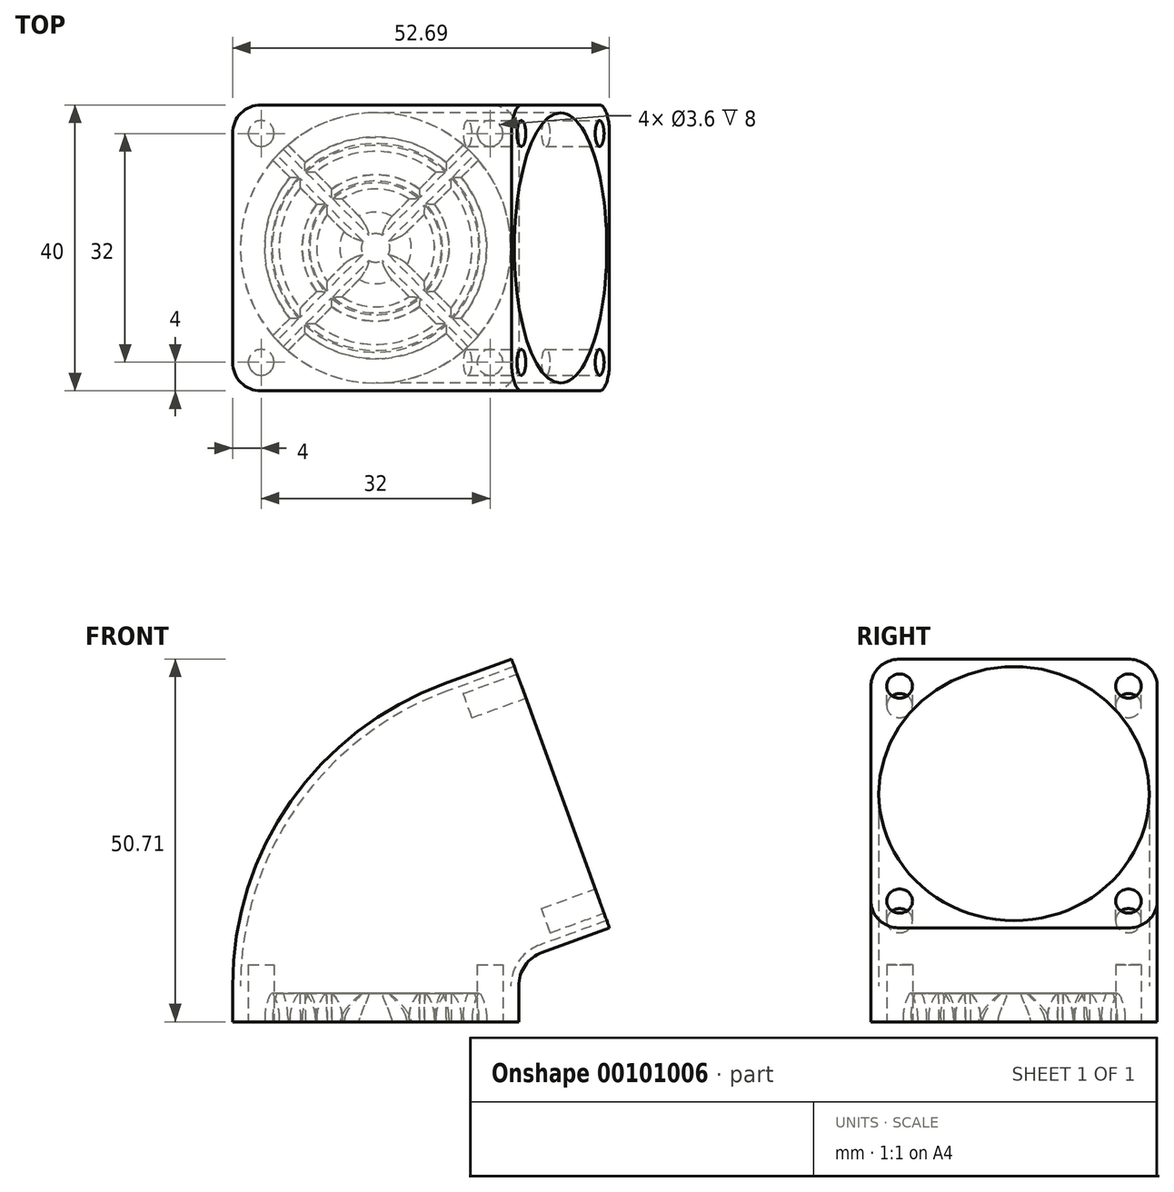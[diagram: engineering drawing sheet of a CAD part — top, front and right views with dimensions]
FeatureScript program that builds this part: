
annotation { "Feature Type Name" : "Feature", "Feature Type Description" : "" }
export const myFeature = defineFeature(function(context is Context, id is Id, definition is map)
    precondition{}
    {
        {
            var Q0;
            Q0=qCreatedBy(makeId("Top.planeOp"),FACE);
            var sketch = newSketch(context, id + "F0", { "sketchPlane" : qUnion([Q0])});
            skLineSegment(sketch, "E0.bottom", {"start": v(16, 20) * mm, "end": v(-16, 20) * mm});
            skLineSegment(sketch, "E0.top", {"start": v(16, -20) * mm, "end": v(-16, -20) * mm});
            skLineSegment(sketch, "E0.left", {"start": v(20, 16) * mm, "end": v(20, -16) * mm});
            skLineSegment(sketch, "E0.right", {"start": v(-20, 16) * mm, "end": v(-20, -16) * mm});
            skPoint(sketch, "E0.middle", {"position": v(0, 0) * mm});
            skPoint(sketch, "E1.visualSharp", {"position": v(-20, 20) * mm});
            skArc(sketch, "E1.filletArc", {"start": v(-16, 20) * mm, "mid": v(-18.83, 18.83) * mm, "end": v(-20, 16) * mm});
            skPoint(sketch, "E2.visualSharp", {"position": v(20, 20) * mm});
            skArc(sketch, "E2.filletArc", {"start": v(20, 16) * mm, "mid": v(18.83, 18.83) * mm, "end": v(16, 20) * mm});
            skPoint(sketch, "E3.visualSharp", {"position": v(20, -20) * mm});
            skArc(sketch, "E3.filletArc", {"start": v(16, -20) * mm, "mid": v(18.83, -18.83) * mm, "end": v(20, -16) * mm});
            skPoint(sketch, "E4.visualSharp", {"position": v(-20, -20) * mm});
            skArc(sketch, "E4.filletArc", {"start": v(-20, -16) * mm, "mid": v(-18.83, -18.83) * mm, "end": v(-16, -20) * mm});
            skCircle(sketch, "E5", {"center": v(16, 16) * mm, "radius": 1.8 * mm});
            skCircle(sketch, "E6", {"center": v(-16, 16) * mm, "radius": 1.8 * mm});
            skCircle(sketch, "E7", {"center": v(-16, -16) * mm, "radius": 1.8 * mm});
            skCircle(sketch, "E8", {"center": v(16, -16) * mm, "radius": 1.8 * mm});
            skCircle(sketch, "E9", {"center": v(0, 0) * mm, "radius": 18.9 * mm});
            skSolve(sketch);
        }
        {
            var Q0;
            Q0=qSketchRegion(id+"F0",true);
            extrude(context, id + "F1", {"entities" : qUnion([Q0]), "depth" : 5 * mm});
        }
        {
            var Q0;
            Q0=qCreatedBy(makeId("Top.planeOp"),FACE);
            var sketch = newSketch(context, id + "F2", { "sketchPlane" : qUnion([Q0])});
            skCircle(sketch, "E10", {"center": v(0, 0) * mm, "radius": 5 * mm});
            skCircle(sketch, "E11", {"center": v(0, 0) * mm, "radius": 8.25 * mm});
            skCircle(sketch, "E12", {"center": v(0, 0) * mm, "radius": 10.25 * mm});
            skCircle(sketch, "E13", {"center": v(0, 0) * mm, "radius": 15.5 * mm});
            skCircle(sketch, "E14", {"center": v(0, 0) * mm, "radius": 13.5 * mm});
            skLineSegment(sketch, "E15", {"start": v(-19.89, 17.77) * mm, "end": v(17.77, -19.89) * mm});
            skLineSegment(sketch, "E16", {"start": v(17.77, -19.89) * mm, "end": v(19.89, -17.77) * mm});
            skLineSegment(sketch, "E17", {"start": v(19.89, -17.77) * mm, "end": v(-17.77, 19.89) * mm});
            skLineSegment(sketch, "E18", {"start": v(-17.77, 19.89) * mm, "end": v(-19.89, 17.77) * mm});
            skLineSegment(sketch, "E19", {"start": v(17.77, 19.89) * mm, "end": v(19.89, 17.77) * mm});
            skLineSegment(sketch, "E20", {"start": v(19.89, 17.77) * mm, "end": v(-17.77, -19.89) * mm});
            skLineSegment(sketch, "E21", {"start": v(-17.77, -19.89) * mm, "end": v(-19.89, -17.77) * mm});
            skLineSegment(sketch, "E22", {"start": v(-19.89, -17.77) * mm, "end": v(17.77, 19.89) * mm});
            skLineSegment(sketch, "E23", {"start": v(0, 0) * mm, "end": v(0, 27.68) * mm, "construction": true});
            skLineSegment(sketch, "E24", {"start": v(0, 0) * mm, "end": v(18.83, 18.83) * mm, "construction": true});
            skLineSegment(sketch, "E25", {"start": v(0, 0) * mm, "end": v(-18.83, 18.83) * mm, "construction": true});
            skSolve(sketch);
        }
        {
            var Q0;
            Q0=qCreatedBy(makeId("Top.planeOp"),FACE);
            var sketch = newSketch(context, id + "F3", { "sketchPlane" : qUnion([Q0])});
            skArc(sketch, "E26.0", {"start": v(-4.43, 2.31) * mm, "mid": v(3.54, -3.54) * mm, "end": v(-2.31, 4.43) * mm});
            skArc(sketch, "E26.1", {"start": v(-6.8, 4.68) * mm, "mid": v(-8.25, 0) * mm, "end": v(-6.8, -4.68) * mm});
            skArc(sketch, "E26.2", {"start": v(-6.1, -8.23) * mm, "mid": v(0, -10.25) * mm, "end": v(6.1, -8.23) * mm});
            skArc(sketch, "E26.3", {"start": v(10.55, -8.43) * mm, "mid": v(13.5, 0) * mm, "end": v(10.55, 8.43) * mm});
            skArc(sketch, "E26.4", {"start": v(11.97, -9.85) * mm, "mid": v(15.5, 0) * mm, "end": v(11.97, 9.85) * mm});
            skLineSegment(sketch, "E26.5", {"start": v(14.38, 12.26) * mm, "end": v(11.97, 9.85) * mm});
            skLineSegment(sketch, "E26.6", {"start": v(-14.38, -12.26) * mm, "end": v(-11.97, -9.85) * mm});
            skLineSegment(sketch, "E26.7", {"start": v(14.38, -12.26) * mm, "end": v(11.97, -9.85) * mm});
            skLineSegment(sketch, "E26.8", {"start": v(-14.38, 12.26) * mm, "end": v(-11.97, 9.85) * mm});
            skLineSegment(sketch, "E27.trimOffspring", {"start": v(-2.31, -4.43) * mm, "end": v(-4.68, -6.8) * mm});
            skLineSegment(sketch, "E28.trimOffspring", {"start": v(2.31, -4.43) * mm, "end": v(4.68, -6.8) * mm});
            skLineSegment(sketch, "E29.trimOffspring", {"start": v(2.31, 4.43) * mm, "end": v(4.68, 6.8) * mm});
            skLineSegment(sketch, "E30.trimOffspring", {"start": v(-2.31, 4.43) * mm, "end": v(-4.68, 6.8) * mm});
            skArc(sketch, "E31.0", {"start": v(-14.38, -12.26) * mm, "mid": v(-13.36, -13.36) * mm, "end": v(-12.26, -14.38) * mm});
            skPoint(sketch, "E32.orphan", {"position": v(-17.77, 19.89) * mm});
            skPoint(sketch, "E33.orphan", {"position": v(-19.89, 17.77) * mm});
            skPoint(sketch, "E34.orphan", {"position": v(19.89, 17.77) * mm});
            skPoint(sketch, "E35.orphan", {"position": v(17.77, 19.89) * mm});
            skArc(sketch, "E36.trimOffspring", {"start": v(-12.26, 14.38) * mm, "mid": v(-13.36, 13.36) * mm, "end": v(-14.38, 12.26) * mm});
            skArc(sketch, "E37.trimOffspring", {"start": v(14.38, 12.26) * mm, "mid": v(13.36, 13.36) * mm, "end": v(12.26, 14.38) * mm});
            skArc(sketch, "E38.trimOffspring", {"start": v(12.26, -14.38) * mm, "mid": v(13.36, -13.36) * mm, "end": v(14.38, -12.26) * mm});
            skLineSegment(sketch, "E39.trimOffspring", {"start": v(10.55, -8.43) * mm, "end": v(8.23, -6.1) * mm});
            skLineSegment(sketch, "E40.trimOffspring", {"start": v(9.85, -11.97) * mm, "end": v(12.26, -14.38) * mm});
            skLineSegment(sketch, "E41.trimOffspring", {"start": v(-9.85, -11.97) * mm, "end": v(-12.26, -14.38) * mm});
            skArc(sketch, "E42.trimOffspring", {"start": v(-8.43, -10.55) * mm, "mid": v(0, -13.5) * mm, "end": v(8.43, -10.55) * mm});
            skLineSegment(sketch, "E43.trimOffspring", {"start": v(-10.55, -8.43) * mm, "end": v(-8.23, -6.1) * mm});
            skPoint(sketch, "E44.orphan", {"position": v(-17.77, -19.89) * mm});
            skPoint(sketch, "E45.orphan", {"position": v(-19.89, -17.77) * mm});
            skLineSegment(sketch, "E46.trimOffspring", {"start": v(-6.8, -4.68) * mm, "end": v(-4.43, -2.31) * mm});
            skArc(sketch, "E47.trimOffspring", {"start": v(-4.68, -6.8) * mm, "mid": v(0, -8.25) * mm, "end": v(4.68, -6.8) * mm});
            skLineSegment(sketch, "E48.trimOffspring", {"start": v(-6.1, -8.23) * mm, "end": v(-8.43, -10.55) * mm});
            skLineSegment(sketch, "E49.trimOffspring", {"start": v(6.1, -8.23) * mm, "end": v(8.43, -10.55) * mm});
            skArc(sketch, "E50.trimOffspring", {"start": v(6.8, -4.68) * mm, "mid": v(8.25, 0) * mm, "end": v(6.8, 4.68) * mm});
            skLineSegment(sketch, "E51.trimOffspring", {"start": v(6.8, -4.68) * mm, "end": v(4.43, -2.31) * mm});
            skArc(sketch, "E52.trimOffspring", {"start": v(8.23, -6.1) * mm, "mid": v(10.25, 0) * mm, "end": v(8.23, 6.1) * mm});
            skArc(sketch, "E53.trimOffspring", {"start": v(4.68, 6.8) * mm, "mid": v(0, 8.25) * mm, "end": v(-4.68, 6.8) * mm});
            skLineSegment(sketch, "E54.trimOffspring", {"start": v(6.8, 4.68) * mm, "end": v(4.43, 2.31) * mm});
            skLineSegment(sketch, "E55.trimOffspring", {"start": v(6.1, 8.23) * mm, "end": v(8.43, 10.55) * mm});
            skArc(sketch, "E56.trimOffspring", {"start": v(6.1, 8.23) * mm, "mid": v(0, 10.25) * mm, "end": v(-6.1, 8.23) * mm});
            skArc(sketch, "E57.trimOffspring", {"start": v(8.43, 10.55) * mm, "mid": v(0, 13.5) * mm, "end": v(-8.43, 10.55) * mm});
            skArc(sketch, "E58.trimOffspring", {"start": v(9.85, 11.97) * mm, "mid": v(0, 15.5) * mm, "end": v(-9.85, 11.97) * mm});
            skLineSegment(sketch, "E59.trimOffspring", {"start": v(10.55, 8.43) * mm, "end": v(8.23, 6.1) * mm});
            skLineSegment(sketch, "E60.trimOffspring", {"start": v(9.85, 11.97) * mm, "end": v(12.26, 14.38) * mm});
            skLineSegment(sketch, "E61.trimOffspring", {"start": v(-6.1, 8.23) * mm, "end": v(-8.43, 10.55) * mm});
            skLineSegment(sketch, "E62.trimOffspring", {"start": v(-6.8, 4.68) * mm, "end": v(-4.43, 2.31) * mm});
            skLineSegment(sketch, "E63.trimOffspring", {"start": v(-10.55, 8.43) * mm, "end": v(-8.23, 6.1) * mm});
            skLineSegment(sketch, "E64.trimOffspring", {"start": v(-9.85, 11.97) * mm, "end": v(-12.26, 14.38) * mm});
            skArc(sketch, "E65.trimOffspring", {"start": v(-11.97, 9.85) * mm, "mid": v(-10.96, -10.96) * mm, "end": v(9.85, -11.97) * mm});
            skArc(sketch, "E66.trimOffspring", {"start": v(-10.55, 8.43) * mm, "mid": v(-13.5, 0) * mm, "end": v(-10.55, -8.43) * mm});
            skArc(sketch, "E67.trimOffspring", {"start": v(-8.23, 6.1) * mm, "mid": v(-10.25, 0) * mm, "end": v(-8.23, -6.1) * mm});
            skPoint(sketch, "E68.orphan", {"position": v(19.89, -17.77) * mm});
            skPoint(sketch, "E69.orphan", {"position": v(17.77, -19.89) * mm});
            skSolve(sketch);
        }
        {
            var Q0;
            Q0=qSketchRegion(id+"F3",true);
            extrude(context, id + "F4", {"entities" : qUnion([Q0]), "operationType" : NewBodyOperationType.ADD, "depth" : 4 * mm});
        }
        {
            var Q0;
            Q0=makeQuery(id+"F4.opExtrude","CAP_EDGE",EDGE,{"disambiguationData":[OSD([sQuery(id+"F3.wireOp",EDGE,"E58.trimOffspring")])],"isStart":false});
            var Q1;
            Q1=makeQuery(id+"F4.opExtrude","CAP_EDGE",EDGE,{"disambiguationData":[OSD([sQuery(id+"F3.wireOp",EDGE,"E57.trimOffspring")])],"isStart":false});
            var Q2;
            Q2=makeQuery(id+"F4.opExtrude","CAP_EDGE",EDGE,{"disambiguationData":[OSD([sQuery(id+"F3.wireOp",EDGE,"E56.trimOffspring")])],"isStart":false});
            var Q3;
            Q3=makeQuery(id+"F4.opExtrude","CAP_EDGE",EDGE,{"disambiguationData":[OSD([sQuery(id+"F3.wireOp",EDGE,"E53.trimOffspring")])],"isStart":false});
            var Q4;
            Q4=makeQuery(id+"F4.opExtrude","CAP_EDGE",EDGE,{"disambiguationData":[OSD([sQuery(id+"F3.wireOp",EDGE,"E26.1")])],"isStart":false});
            var Q5;
            Q5=makeQuery(id+"F4.opExtrude","CAP_EDGE",EDGE,{"disambiguationData":[OSD([sQuery(id+"F3.wireOp",EDGE,"E67.trimOffspring")])],"isStart":false});
            var Q6;
            Q6=makeQuery(id+"F4.opExtrude","CAP_EDGE",EDGE,{"disambiguationData":[OSD([sQuery(id+"F3.wireOp",EDGE,"E66.trimOffspring")])],"isStart":false});
            var Q7;
            {var subQ0=sQuery(id+"F3.wireOp",EDGE,"E65.trimOffspring");Q7=makeQuery(id+"F4.opExtrude","CAP_EDGE",EDGE,{"disambiguationData":[OSD([subQ0]),TDD([makeQuery(id+"F3.imprint","IMPRINT",EDGE,{"disambiguationData":[TD([[makeQuery(id+"F3.imprint","INTERSECT",VERTEX,{"derivedFrom":[sQuery(id+"F3.wireOp",EDGE,"E26.6"),subQ0]}),1.0]])],"derivedFrom":subQ0})])],"isStart":false});}
            var Q8;
            Q8=makeQuery(id+"F4.opExtrude","CAP_EDGE",EDGE,{"disambiguationData":[OSD([sQuery(id+"F3.wireOp",EDGE,"E50.trimOffspring")])],"isStart":false});
            var Q9;
            Q9=makeQuery(id+"F4.opExtrude","CAP_EDGE",EDGE,{"disambiguationData":[OSD([sQuery(id+"F3.wireOp",EDGE,"E26.3")])],"isStart":false});
            var Q10;
            Q10=makeQuery(id+"F4.opExtrude","CAP_EDGE",EDGE,{"disambiguationData":[OSD([sQuery(id+"F3.wireOp",EDGE,"E26.4")])],"isStart":false});
            var Q11;
            Q11=makeQuery(id+"F4.opExtrude","CAP_EDGE",EDGE,{"disambiguationData":[OSD([sQuery(id+"F3.wireOp",EDGE,"E52.trimOffspring")])],"isStart":false});
            var Q12;
            {var subQ0=sQuery(id+"F3.wireOp",EDGE,"E65.trimOffspring");Q12=makeQuery(id+"F4.opExtrude","CAP_EDGE",EDGE,{"disambiguationData":[OSD([subQ0]),TDD([makeQuery(id+"F3.imprint","IMPRINT",EDGE,{"disambiguationData":[TD([[makeQuery(id+"F3.imprint","INTERSECT",VERTEX,{"derivedFrom":[sQuery(id+"F3.wireOp",EDGE,"E40.trimOffspring"),subQ0]}),1.0]])],"derivedFrom":subQ0})])],"isStart":false});}
            var Q13;
            Q13=makeQuery(id+"F4.opExtrude","CAP_EDGE",EDGE,{"disambiguationData":[OSD([sQuery(id+"F3.wireOp",EDGE,"E42.trimOffspring")])],"isStart":false});
            var Q14;
            Q14=makeQuery(id+"F4.opExtrude","CAP_EDGE",EDGE,{"disambiguationData":[OSD([sQuery(id+"F3.wireOp",EDGE,"E26.2")])],"isStart":false});
            var Q15;
            Q15=makeQuery(id+"F4.opExtrude","CAP_EDGE",EDGE,{"disambiguationData":[OSD([sQuery(id+"F3.wireOp",EDGE,"E47.trimOffspring")])],"isStart":false});
            var Q16;
            Q16=makeQuery(id+"F4.opExtrude","CAP_EDGE",EDGE,{"disambiguationData":[OSD([sQuery(id+"F3.wireOp",EDGE,"E61.trimOffspring")])],"isStart":false});
            var Q17;
            Q17=makeQuery(id+"F4.opExtrude","CAP_EDGE",EDGE,{"disambiguationData":[OSD([sQuery(id+"F3.wireOp",EDGE,"E63.trimOffspring")])],"isStart":false});
            var Q18;
            Q18=makeQuery(id+"F4.opExtrude","CAP_EDGE",EDGE,{"disambiguationData":[OSD([sQuery(id+"F3.wireOp",EDGE,"E26.8")])],"isStart":false});
            var Q19;
            Q19=makeQuery(id+"F4.opExtrude","CAP_EDGE",EDGE,{"disambiguationData":[OSD([sQuery(id+"F3.wireOp",EDGE,"E64.trimOffspring")])],"isStart":false});
            var Q20;
            Q20=makeQuery(id+"F4.opExtrude","CAP_EDGE",EDGE,{"disambiguationData":[OSD([sQuery(id+"F3.wireOp",EDGE,"E30.trimOffspring")])],"isStart":false});
            var Q21;
            Q21=makeQuery(id+"F4.opExtrude","CAP_EDGE",EDGE,{"disambiguationData":[OSD([sQuery(id+"F3.wireOp",EDGE,"E62.trimOffspring")])],"isStart":false});
            var Q22;
            Q22=makeQuery(id+"F4.opExtrude","CAP_EDGE",EDGE,{"disambiguationData":[OSD([sQuery(id+"F3.wireOp",EDGE,"E27.trimOffspring")])],"isStart":false});
            var Q23;
            Q23=makeQuery(id+"F4.opExtrude","CAP_EDGE",EDGE,{"disambiguationData":[OSD([sQuery(id+"F3.wireOp",EDGE,"E46.trimOffspring")])],"isStart":false});
            var Q24;
            Q24=makeQuery(id+"F4.opExtrude","CAP_EDGE",EDGE,{"disambiguationData":[OSD([sQuery(id+"F3.wireOp",EDGE,"E43.trimOffspring")])],"isStart":false});
            var Q25;
            Q25=makeQuery(id+"F4.opExtrude","CAP_EDGE",EDGE,{"disambiguationData":[OSD([sQuery(id+"F3.wireOp",EDGE,"E48.trimOffspring")])],"isStart":false});
            var Q26;
            Q26=makeQuery(id+"F4.opExtrude","CAP_EDGE",EDGE,{"disambiguationData":[OSD([sQuery(id+"F3.wireOp",EDGE,"E41.trimOffspring")])],"isStart":false});
            var Q27;
            Q27=makeQuery(id+"F4.opExtrude","CAP_EDGE",EDGE,{"disambiguationData":[OSD([sQuery(id+"F3.wireOp",EDGE,"E26.6")])],"isStart":false});
            var Q28;
            Q28=makeQuery(id+"F4.opExtrude","CAP_EDGE",EDGE,{"disambiguationData":[OSD([sQuery(id+"F3.wireOp",EDGE,"E28.trimOffspring")])],"isStart":false});
            var Q29;
            Q29=makeQuery(id+"F4.opExtrude","CAP_EDGE",EDGE,{"disambiguationData":[OSD([sQuery(id+"F3.wireOp",EDGE,"E51.trimOffspring")])],"isStart":false});
            var Q30;
            Q30=makeQuery(id+"F4.opExtrude","CAP_EDGE",EDGE,{"disambiguationData":[OSD([sQuery(id+"F3.wireOp",EDGE,"E49.trimOffspring")])],"isStart":false});
            var Q31;
            Q31=makeQuery(id+"F4.opExtrude","CAP_EDGE",EDGE,{"disambiguationData":[OSD([sQuery(id+"F3.wireOp",EDGE,"E39.trimOffspring")])],"isStart":false});
            var Q32;
            Q32=makeQuery(id+"F4.opExtrude","CAP_EDGE",EDGE,{"disambiguationData":[OSD([sQuery(id+"F3.wireOp",EDGE,"E40.trimOffspring")])],"isStart":false});
            var Q33;
            Q33=makeQuery(id+"F4.opExtrude","CAP_EDGE",EDGE,{"disambiguationData":[OSD([sQuery(id+"F3.wireOp",EDGE,"E26.7")])],"isStart":false});
            var Q34;
            Q34=makeQuery(id+"F4.opExtrude","CAP_EDGE",EDGE,{"disambiguationData":[OSD([sQuery(id+"F3.wireOp",EDGE,"E54.trimOffspring")])],"isStart":false});
            var Q35;
            Q35=makeQuery(id+"F4.opExtrude","CAP_EDGE",EDGE,{"disambiguationData":[OSD([sQuery(id+"F3.wireOp",EDGE,"E29.trimOffspring")])],"isStart":false});
            var Q36;
            Q36=makeQuery(id+"F4.opExtrude","CAP_EDGE",EDGE,{"disambiguationData":[OSD([sQuery(id+"F3.wireOp",EDGE,"E59.trimOffspring")])],"isStart":false});
            var Q37;
            Q37=makeQuery(id+"F4.opExtrude","CAP_EDGE",EDGE,{"disambiguationData":[OSD([sQuery(id+"F3.wireOp",EDGE,"E55.trimOffspring")])],"isStart":false});
            var Q38;
            Q38=makeQuery(id+"F4.opExtrude","CAP_EDGE",EDGE,{"disambiguationData":[OSD([sQuery(id+"F3.wireOp",EDGE,"E60.trimOffspring")])],"isStart":false});
            var Q39;
            Q39=makeQuery(id+"F4.opExtrude","CAP_EDGE",EDGE,{"disambiguationData":[OSD([sQuery(id+"F3.wireOp",EDGE,"E26.5")])],"isStart":false});
            chamfer(context, id + "F5", {"entities" : qUnion([Q0, Q1, Q2, Q3, Q4, Q5, Q6, Q7, Q8, Q9, Q10, Q11, Q12, Q13, Q14, Q15, Q16, Q17, Q18, Q19, Q20, Q21, Q22, Q23, Q24, Q25, Q26, Q27, Q28, Q29, Q30, Q31, Q32, Q33, Q34, Q35, Q36, Q37, Q38, Q39]), "width" : .9 * mm, "tangentPropagation" : true});
        }
        {
            var Q0;
            {var subQ0=sQuery(id+"F3.wireOp",EDGE,"E26.0");Q0=makeQuery(id+"F4.opExtrude","CAP_EDGE",EDGE,{"disambiguationData":[OSD([subQ0]),TDD([makeQuery(id+"F3.imprint","IMPRINT",EDGE,{"disambiguationData":[TD([[makeQuery(id+"F3.imprint","INTERSECT",VERTEX,{"derivedFrom":[subQ0,sQuery(id+"F3.wireOp",EDGE,"E27.trimOffspring")]}),-1.0]])],"derivedFrom":subQ0})])],"isStart":false});}
            var Q1;
            {var subQ0=sQuery(id+"F3.wireOp",EDGE,"E26.0");Q1=makeQuery(id+"F4.opExtrude","CAP_EDGE",EDGE,{"disambiguationData":[OSD([subQ0]),TDD([makeQuery(id+"F3.imprint","IMPRINT",EDGE,{"disambiguationData":[TD([[makeQuery(id+"F3.imprint","INTERSECT",VERTEX,{"derivedFrom":[subQ0,sQuery(id+"F3.wireOp",EDGE,"E51.trimOffspring")]}),-1.0]])],"derivedFrom":subQ0})])],"isStart":false});}
            var Q2;
            {var subQ0=sQuery(id+"F3.wireOp",EDGE,"E26.0");Q2=makeQuery(id+"F4.opExtrude","CAP_EDGE",EDGE,{"disambiguationData":[OSD([subQ0]),TDD([makeQuery(id+"F3.imprint","IMPRINT",EDGE,{"disambiguationData":[TD([[makeQuery(id+"F3.imprint","INTERSECT",VERTEX,{"derivedFrom":[subQ0,sQuery(id+"F3.wireOp",EDGE,"E30.trimOffspring")]}),1.0]])],"derivedFrom":subQ0})])],"isStart":false});}
            var Q3;
            {var subQ0=sQuery(id+"F3.wireOp",EDGE,"E26.0");Q3=makeQuery(id+"F4.opExtrude","CAP_EDGE",EDGE,{"disambiguationData":[OSD([subQ0]),TDD([makeQuery(id+"F3.imprint","IMPRINT",EDGE,{"disambiguationData":[TD([[makeQuery(id+"F3.imprint","INTERSECT",VERTEX,{"derivedFrom":[subQ0,sQuery(id+"F3.wireOp",EDGE,"E62.trimOffspring")]}),-1.0]])],"derivedFrom":subQ0})])],"isStart":false});}
            chamfer(context, id + "F6", {"entities" : qUnion([Q0, Q1, Q2, Q3]), "width" : 3 * mm, "tangentPropagation" : true});
        }
        {
            var Q0;
            {var subQ0=sQuery(id+"F3.wireOp",EDGE,"E26.8");Q0=makeQuery(id+"F5.opChamfer","BLEND_EDGE",EDGE,{"blendedFrom":[makeQuery(id+"F4.opExtrude","CAP_EDGE",EDGE,{"disambiguationData":[OSD([subQ0])],"isStart":false}),makeQuery(id+"F4.opExtrude","SWEPT_FACE",FACE,{"disambiguationData":[OSD([subQ0])]})],"blendedInto":[makeQuery(id+"F4.opExtrude","SWEPT_FACE",FACE,{"disambiguationData":[OSD([subQ0])]})]});}
            var Q1;
            {var subQ0=sQuery(id+"F3.wireOp",EDGE,"E63.trimOffspring");Q1=makeQuery(id+"F5.opChamfer","BLEND_EDGE",EDGE,{"blendedFrom":[makeQuery(id+"F4.opExtrude","CAP_EDGE",EDGE,{"disambiguationData":[OSD([subQ0])],"isStart":false}),makeQuery(id+"F4.opExtrude","SWEPT_FACE",FACE,{"disambiguationData":[OSD([subQ0])]})],"blendedInto":[makeQuery(id+"F4.opExtrude","SWEPT_FACE",FACE,{"disambiguationData":[OSD([subQ0])]})]});}
            var Q2;
            {var subQ0=sQuery(id+"F3.wireOp",EDGE,"E62.trimOffspring");Q2=makeQuery(id+"F5.opChamfer","BLEND_EDGE",EDGE,{"blendedFrom":[makeQuery(id+"F4.opExtrude","CAP_EDGE",EDGE,{"disambiguationData":[OSD([subQ0])],"isStart":false}),makeQuery(id+"F4.opExtrude","SWEPT_FACE",FACE,{"disambiguationData":[OSD([subQ0])]})],"blendedInto":[makeQuery(id+"F4.opExtrude","SWEPT_FACE",FACE,{"disambiguationData":[OSD([subQ0])]})]});}
            var Q3;
            {var subQ0=sQuery(id+"F3.wireOp",EDGE,"E30.trimOffspring");Q3=makeQuery(id+"F5.opChamfer","BLEND_EDGE",EDGE,{"blendedFrom":[makeQuery(id+"F4.opExtrude","CAP_EDGE",EDGE,{"disambiguationData":[OSD([subQ0])],"isStart":false}),makeQuery(id+"F4.opExtrude","SWEPT_FACE",FACE,{"disambiguationData":[OSD([subQ0])]})],"blendedInto":[makeQuery(id+"F4.opExtrude","SWEPT_FACE",FACE,{"disambiguationData":[OSD([subQ0])]})]});}
            var Q4;
            {var subQ0=sQuery(id+"F3.wireOp",EDGE,"E61.trimOffspring");Q4=makeQuery(id+"F5.opChamfer","BLEND_EDGE",EDGE,{"blendedFrom":[makeQuery(id+"F4.opExtrude","CAP_EDGE",EDGE,{"disambiguationData":[OSD([subQ0])],"isStart":false}),makeQuery(id+"F4.opExtrude","SWEPT_FACE",FACE,{"disambiguationData":[OSD([subQ0])]})],"blendedInto":[makeQuery(id+"F4.opExtrude","SWEPT_FACE",FACE,{"disambiguationData":[OSD([subQ0])]})]});}
            var Q5;
            {var subQ0=sQuery(id+"F3.wireOp",EDGE,"E64.trimOffspring");Q5=makeQuery(id+"F5.opChamfer","BLEND_EDGE",EDGE,{"blendedFrom":[makeQuery(id+"F4.opExtrude","CAP_EDGE",EDGE,{"disambiguationData":[OSD([subQ0])],"isStart":false}),makeQuery(id+"F4.opExtrude","SWEPT_FACE",FACE,{"disambiguationData":[OSD([subQ0])]})],"blendedInto":[makeQuery(id+"F4.opExtrude","SWEPT_FACE",FACE,{"disambiguationData":[OSD([subQ0])]})]});}
            var Q6;
            {var subQ0=sQuery(id+"F3.wireOp",EDGE,"E54.trimOffspring");Q6=makeQuery(id+"F5.opChamfer","BLEND_EDGE",EDGE,{"blendedFrom":[makeQuery(id+"F4.opExtrude","CAP_EDGE",EDGE,{"disambiguationData":[OSD([subQ0])],"isStart":false}),makeQuery(id+"F4.opExtrude","SWEPT_FACE",FACE,{"disambiguationData":[OSD([subQ0])]})],"blendedInto":[makeQuery(id+"F4.opExtrude","SWEPT_FACE",FACE,{"disambiguationData":[OSD([subQ0])]})]});}
            var Q7;
            {var subQ0=sQuery(id+"F3.wireOp",EDGE,"E29.trimOffspring");Q7=makeQuery(id+"F5.opChamfer","BLEND_EDGE",EDGE,{"blendedFrom":[makeQuery(id+"F4.opExtrude","CAP_EDGE",EDGE,{"disambiguationData":[OSD([subQ0])],"isStart":false}),makeQuery(id+"F4.opExtrude","SWEPT_FACE",FACE,{"disambiguationData":[OSD([subQ0])]})],"blendedInto":[makeQuery(id+"F4.opExtrude","SWEPT_FACE",FACE,{"disambiguationData":[OSD([subQ0])]})]});}
            var Q8;
            {var subQ0=sQuery(id+"F3.wireOp",EDGE,"E55.trimOffspring");Q8=makeQuery(id+"F5.opChamfer","BLEND_EDGE",EDGE,{"blendedFrom":[makeQuery(id+"F4.opExtrude","CAP_EDGE",EDGE,{"disambiguationData":[OSD([subQ0])],"isStart":false}),makeQuery(id+"F4.opExtrude","SWEPT_FACE",FACE,{"disambiguationData":[OSD([subQ0])]})],"blendedInto":[makeQuery(id+"F4.opExtrude","SWEPT_FACE",FACE,{"disambiguationData":[OSD([subQ0])]})]});}
            var Q9;
            {var subQ0=sQuery(id+"F3.wireOp",EDGE,"E59.trimOffspring");Q9=makeQuery(id+"F5.opChamfer","BLEND_EDGE",EDGE,{"blendedFrom":[makeQuery(id+"F4.opExtrude","CAP_EDGE",EDGE,{"disambiguationData":[OSD([subQ0])],"isStart":false}),makeQuery(id+"F4.opExtrude","SWEPT_FACE",FACE,{"disambiguationData":[OSD([subQ0])]})],"blendedInto":[makeQuery(id+"F4.opExtrude","SWEPT_FACE",FACE,{"disambiguationData":[OSD([subQ0])]})]});}
            var Q10;
            {var subQ0=sQuery(id+"F3.wireOp",EDGE,"E26.5");Q10=makeQuery(id+"F5.opChamfer","BLEND_EDGE",EDGE,{"blendedFrom":[makeQuery(id+"F4.opExtrude","CAP_EDGE",EDGE,{"disambiguationData":[OSD([subQ0])],"isStart":false}),makeQuery(id+"F4.opExtrude","SWEPT_FACE",FACE,{"disambiguationData":[OSD([subQ0])]})],"blendedInto":[makeQuery(id+"F4.opExtrude","SWEPT_FACE",FACE,{"disambiguationData":[OSD([subQ0])]})]});}
            var Q11;
            {var subQ0=sQuery(id+"F3.wireOp",EDGE,"E60.trimOffspring");Q11=makeQuery(id+"F5.opChamfer","BLEND_EDGE",EDGE,{"blendedFrom":[makeQuery(id+"F4.opExtrude","CAP_EDGE",EDGE,{"disambiguationData":[OSD([subQ0])],"isStart":false}),makeQuery(id+"F4.opExtrude","SWEPT_FACE",FACE,{"disambiguationData":[OSD([subQ0])]})],"blendedInto":[makeQuery(id+"F4.opExtrude","SWEPT_FACE",FACE,{"disambiguationData":[OSD([subQ0])]})]});}
            var Q12;
            {var subQ0=sQuery(id+"F3.wireOp",EDGE,"E51.trimOffspring");Q12=makeQuery(id+"F5.opChamfer","BLEND_EDGE",EDGE,{"blendedFrom":[makeQuery(id+"F4.opExtrude","CAP_EDGE",EDGE,{"disambiguationData":[OSD([subQ0])],"isStart":false}),makeQuery(id+"F4.opExtrude","SWEPT_FACE",FACE,{"disambiguationData":[OSD([subQ0])]})],"blendedInto":[makeQuery(id+"F4.opExtrude","SWEPT_FACE",FACE,{"disambiguationData":[OSD([subQ0])]})]});}
            var Q13;
            {var subQ0=sQuery(id+"F3.wireOp",EDGE,"E39.trimOffspring");Q13=makeQuery(id+"F5.opChamfer","BLEND_EDGE",EDGE,{"blendedFrom":[makeQuery(id+"F4.opExtrude","CAP_EDGE",EDGE,{"disambiguationData":[OSD([subQ0])],"isStart":false}),makeQuery(id+"F4.opExtrude","SWEPT_FACE",FACE,{"disambiguationData":[OSD([subQ0])]})],"blendedInto":[makeQuery(id+"F4.opExtrude","SWEPT_FACE",FACE,{"disambiguationData":[OSD([subQ0])]})]});}
            var Q14;
            {var subQ0=sQuery(id+"F3.wireOp",EDGE,"E26.7");Q14=makeQuery(id+"F5.opChamfer","BLEND_EDGE",EDGE,{"blendedFrom":[makeQuery(id+"F4.opExtrude","CAP_EDGE",EDGE,{"disambiguationData":[OSD([subQ0])],"isStart":false}),makeQuery(id+"F4.opExtrude","SWEPT_FACE",FACE,{"disambiguationData":[OSD([subQ0])]})],"blendedInto":[makeQuery(id+"F4.opExtrude","SWEPT_FACE",FACE,{"disambiguationData":[OSD([subQ0])]})]});}
            var Q15;
            {var subQ0=sQuery(id+"F3.wireOp",EDGE,"E40.trimOffspring");Q15=makeQuery(id+"F5.opChamfer","BLEND_EDGE",EDGE,{"blendedFrom":[makeQuery(id+"F4.opExtrude","CAP_EDGE",EDGE,{"disambiguationData":[OSD([subQ0])],"isStart":false}),makeQuery(id+"F4.opExtrude","SWEPT_FACE",FACE,{"disambiguationData":[OSD([subQ0])]})],"blendedInto":[makeQuery(id+"F4.opExtrude","SWEPT_FACE",FACE,{"disambiguationData":[OSD([subQ0])]})]});}
            var Q16;
            {var subQ0=sQuery(id+"F3.wireOp",EDGE,"E49.trimOffspring");Q16=makeQuery(id+"F5.opChamfer","BLEND_EDGE",EDGE,{"blendedFrom":[makeQuery(id+"F4.opExtrude","CAP_EDGE",EDGE,{"disambiguationData":[OSD([subQ0])],"isStart":false}),makeQuery(id+"F4.opExtrude","SWEPT_FACE",FACE,{"disambiguationData":[OSD([subQ0])]})],"blendedInto":[makeQuery(id+"F4.opExtrude","SWEPT_FACE",FACE,{"disambiguationData":[OSD([subQ0])]})]});}
            var Q17;
            {var subQ0=sQuery(id+"F3.wireOp",EDGE,"E28.trimOffspring");Q17=makeQuery(id+"F5.opChamfer","BLEND_EDGE",EDGE,{"blendedFrom":[makeQuery(id+"F4.opExtrude","CAP_EDGE",EDGE,{"disambiguationData":[OSD([subQ0])],"isStart":false}),makeQuery(id+"F4.opExtrude","SWEPT_FACE",FACE,{"disambiguationData":[OSD([subQ0])]})],"blendedInto":[makeQuery(id+"F4.opExtrude","SWEPT_FACE",FACE,{"disambiguationData":[OSD([subQ0])]})]});}
            var Q18;
            {var subQ0=sQuery(id+"F3.wireOp",EDGE,"E27.trimOffspring");Q18=makeQuery(id+"F5.opChamfer","BLEND_EDGE",EDGE,{"blendedFrom":[makeQuery(id+"F4.opExtrude","CAP_EDGE",EDGE,{"disambiguationData":[OSD([subQ0])],"isStart":false}),makeQuery(id+"F4.opExtrude","SWEPT_FACE",FACE,{"disambiguationData":[OSD([subQ0])]})],"blendedInto":[makeQuery(id+"F4.opExtrude","SWEPT_FACE",FACE,{"disambiguationData":[OSD([subQ0])]})]});}
            var Q19;
            {var subQ0=sQuery(id+"F3.wireOp",EDGE,"E46.trimOffspring");Q19=makeQuery(id+"F5.opChamfer","BLEND_EDGE",EDGE,{"blendedFrom":[makeQuery(id+"F4.opExtrude","CAP_EDGE",EDGE,{"disambiguationData":[OSD([subQ0])],"isStart":false}),makeQuery(id+"F4.opExtrude","SWEPT_FACE",FACE,{"disambiguationData":[OSD([subQ0])]})],"blendedInto":[makeQuery(id+"F4.opExtrude","SWEPT_FACE",FACE,{"disambiguationData":[OSD([subQ0])]})]});}
            var Q20;
            {var subQ0=sQuery(id+"F3.wireOp",EDGE,"E43.trimOffspring");Q20=makeQuery(id+"F5.opChamfer","BLEND_EDGE",EDGE,{"blendedFrom":[makeQuery(id+"F4.opExtrude","CAP_EDGE",EDGE,{"disambiguationData":[OSD([subQ0])],"isStart":false}),makeQuery(id+"F4.opExtrude","SWEPT_FACE",FACE,{"disambiguationData":[OSD([subQ0])]})],"blendedInto":[makeQuery(id+"F4.opExtrude","SWEPT_FACE",FACE,{"disambiguationData":[OSD([subQ0])]})]});}
            var Q21;
            {var subQ0=sQuery(id+"F3.wireOp",EDGE,"E48.trimOffspring");Q21=makeQuery(id+"F5.opChamfer","BLEND_EDGE",EDGE,{"blendedFrom":[makeQuery(id+"F4.opExtrude","CAP_EDGE",EDGE,{"disambiguationData":[OSD([subQ0])],"isStart":false}),makeQuery(id+"F4.opExtrude","SWEPT_FACE",FACE,{"disambiguationData":[OSD([subQ0])]})],"blendedInto":[makeQuery(id+"F4.opExtrude","SWEPT_FACE",FACE,{"disambiguationData":[OSD([subQ0])]})]});}
            var Q22;
            {var subQ0=sQuery(id+"F3.wireOp",EDGE,"E41.trimOffspring");Q22=makeQuery(id+"F5.opChamfer","BLEND_EDGE",EDGE,{"blendedFrom":[makeQuery(id+"F4.opExtrude","CAP_EDGE",EDGE,{"disambiguationData":[OSD([subQ0])],"isStart":false}),makeQuery(id+"F4.opExtrude","SWEPT_FACE",FACE,{"disambiguationData":[OSD([subQ0])]})],"blendedInto":[makeQuery(id+"F4.opExtrude","SWEPT_FACE",FACE,{"disambiguationData":[OSD([subQ0])]})]});}
            var Q23;
            {var subQ0=sQuery(id+"F3.wireOp",EDGE,"E26.6");Q23=makeQuery(id+"F5.opChamfer","BLEND_EDGE",EDGE,{"blendedFrom":[makeQuery(id+"F4.opExtrude","CAP_EDGE",EDGE,{"disambiguationData":[OSD([subQ0])],"isStart":false}),makeQuery(id+"F4.opExtrude","SWEPT_FACE",FACE,{"disambiguationData":[OSD([subQ0])]})],"blendedInto":[makeQuery(id+"F4.opExtrude","SWEPT_FACE",FACE,{"disambiguationData":[OSD([subQ0])]})]});}
            var Q24;
            {var subQ0=sQuery(id+"F3.wireOp",EDGE,"E47.trimOffspring");Q24=makeQuery(id+"F5.opChamfer","BLEND_EDGE",EDGE,{"blendedFrom":[makeQuery(id+"F4.opExtrude","CAP_EDGE",EDGE,{"disambiguationData":[OSD([subQ0])],"isStart":false}),makeQuery(id+"F4.opExtrude","SWEPT_FACE",FACE,{"disambiguationData":[OSD([subQ0])]})],"blendedInto":[makeQuery(id+"F4.opExtrude","SWEPT_FACE",FACE,{"disambiguationData":[OSD([subQ0])]})]});}
            var Q25;
            {var subQ0=sQuery(id+"F3.wireOp",EDGE,"E26.2");Q25=makeQuery(id+"F5.opChamfer","BLEND_EDGE",EDGE,{"blendedFrom":[makeQuery(id+"F4.opExtrude","CAP_EDGE",EDGE,{"disambiguationData":[OSD([subQ0])],"isStart":false}),makeQuery(id+"F4.opExtrude","SWEPT_FACE",FACE,{"disambiguationData":[OSD([subQ0])]})],"blendedInto":[makeQuery(id+"F4.opExtrude","SWEPT_FACE",FACE,{"disambiguationData":[OSD([subQ0])]})]});}
            var Q26;
            {var subQ0=sQuery(id+"F3.wireOp",EDGE,"E65.trimOffspring");var subQ1=makeQuery(id+"F3.imprint","IMPRINT",EDGE,{"disambiguationData":[TD([[makeQuery(id+"F3.imprint","INTERSECT",VERTEX,{"derivedFrom":[sQuery(id+"F3.wireOp",EDGE,"E40.trimOffspring"),subQ0]}),1.0]])],"derivedFrom":subQ0});Q26=makeQuery(id+"F5.opChamfer","BLEND_EDGE",EDGE,{"blendedFrom":[makeQuery(id+"F4.opExtrude","CAP_EDGE",EDGE,{"disambiguationData":[OSD([subQ0]),TDD([subQ1])],"isStart":false}),makeQuery(id+"F4.opExtrude","SWEPT_FACE",FACE,{"disambiguationData":[OSD([subQ0]),TDD([subQ1])]})],"blendedInto":[makeQuery(id+"F4.opExtrude","SWEPT_FACE",FACE,{"disambiguationData":[OSD([subQ0]),TDD([subQ1])]})]});}
            var Q27;
            {var subQ0=sQuery(id+"F3.wireOp",EDGE,"E42.trimOffspring");Q27=makeQuery(id+"F5.opChamfer","BLEND_EDGE",EDGE,{"blendedFrom":[makeQuery(id+"F4.opExtrude","CAP_EDGE",EDGE,{"disambiguationData":[OSD([subQ0])],"isStart":false}),makeQuery(id+"F4.opExtrude","SWEPT_FACE",FACE,{"disambiguationData":[OSD([subQ0])]})],"blendedInto":[makeQuery(id+"F4.opExtrude","SWEPT_FACE",FACE,{"disambiguationData":[OSD([subQ0])]})]});}
            var Q28;
            {var subQ0=sQuery(id+"F3.wireOp",EDGE,"E66.trimOffspring");Q28=makeQuery(id+"F5.opChamfer","BLEND_EDGE",EDGE,{"blendedFrom":[makeQuery(id+"F4.opExtrude","CAP_EDGE",EDGE,{"disambiguationData":[OSD([subQ0])],"isStart":false}),makeQuery(id+"F4.opExtrude","SWEPT_FACE",FACE,{"disambiguationData":[OSD([subQ0])]})],"blendedInto":[makeQuery(id+"F4.opExtrude","SWEPT_FACE",FACE,{"disambiguationData":[OSD([subQ0])]})]});}
            var Q29;
            {var subQ0=sQuery(id+"F3.wireOp",EDGE,"E26.1");Q29=makeQuery(id+"F5.opChamfer","BLEND_EDGE",EDGE,{"blendedFrom":[makeQuery(id+"F4.opExtrude","CAP_EDGE",EDGE,{"disambiguationData":[OSD([subQ0])],"isStart":false}),makeQuery(id+"F4.opExtrude","SWEPT_FACE",FACE,{"disambiguationData":[OSD([subQ0])]})],"blendedInto":[makeQuery(id+"F4.opExtrude","SWEPT_FACE",FACE,{"disambiguationData":[OSD([subQ0])]})]});}
            var Q30;
            {var subQ0=sQuery(id+"F3.wireOp",EDGE,"E67.trimOffspring");Q30=makeQuery(id+"F5.opChamfer","BLEND_EDGE",EDGE,{"blendedFrom":[makeQuery(id+"F4.opExtrude","CAP_EDGE",EDGE,{"disambiguationData":[OSD([subQ0])],"isStart":false}),makeQuery(id+"F4.opExtrude","SWEPT_FACE",FACE,{"disambiguationData":[OSD([subQ0])]})],"blendedInto":[makeQuery(id+"F4.opExtrude","SWEPT_FACE",FACE,{"disambiguationData":[OSD([subQ0])]})]});}
            var Q31;
            {var subQ0=sQuery(id+"F3.wireOp",EDGE,"E65.trimOffspring");var subQ1=makeQuery(id+"F3.imprint","IMPRINT",EDGE,{"disambiguationData":[TD([[makeQuery(id+"F3.imprint","INTERSECT",VERTEX,{"derivedFrom":[sQuery(id+"F3.wireOp",EDGE,"E26.6"),subQ0]}),1.0]])],"derivedFrom":subQ0});Q31=makeQuery(id+"F5.opChamfer","BLEND_EDGE",EDGE,{"blendedFrom":[makeQuery(id+"F4.opExtrude","CAP_EDGE",EDGE,{"disambiguationData":[OSD([subQ0]),TDD([subQ1])],"isStart":false}),makeQuery(id+"F4.opExtrude","SWEPT_FACE",FACE,{"disambiguationData":[OSD([subQ0]),TDD([subQ1])]})],"blendedInto":[makeQuery(id+"F4.opExtrude","SWEPT_FACE",FACE,{"disambiguationData":[OSD([subQ0]),TDD([subQ1])]})]});}
            var Q32;
            {var subQ0=sQuery(id+"F3.wireOp",EDGE,"E53.trimOffspring");Q32=makeQuery(id+"F5.opChamfer","BLEND_EDGE",EDGE,{"blendedFrom":[makeQuery(id+"F4.opExtrude","CAP_EDGE",EDGE,{"disambiguationData":[OSD([subQ0])],"isStart":false}),makeQuery(id+"F4.opExtrude","SWEPT_FACE",FACE,{"disambiguationData":[OSD([subQ0])]})],"blendedInto":[makeQuery(id+"F4.opExtrude","SWEPT_FACE",FACE,{"disambiguationData":[OSD([subQ0])]})]});}
            var Q33;
            {var subQ0=sQuery(id+"F3.wireOp",EDGE,"E57.trimOffspring");Q33=makeQuery(id+"F5.opChamfer","BLEND_EDGE",EDGE,{"blendedFrom":[makeQuery(id+"F4.opExtrude","CAP_EDGE",EDGE,{"disambiguationData":[OSD([subQ0])],"isStart":false}),makeQuery(id+"F4.opExtrude","SWEPT_FACE",FACE,{"disambiguationData":[OSD([subQ0])]})],"blendedInto":[makeQuery(id+"F4.opExtrude","SWEPT_FACE",FACE,{"disambiguationData":[OSD([subQ0])]})]});}
            var Q34;
            {var subQ0=sQuery(id+"F3.wireOp",EDGE,"E58.trimOffspring");Q34=makeQuery(id+"F5.opChamfer","BLEND_EDGE",EDGE,{"blendedFrom":[makeQuery(id+"F4.opExtrude","CAP_EDGE",EDGE,{"disambiguationData":[OSD([subQ0])],"isStart":false}),makeQuery(id+"F4.opExtrude","SWEPT_FACE",FACE,{"disambiguationData":[OSD([subQ0])]})],"blendedInto":[makeQuery(id+"F4.opExtrude","SWEPT_FACE",FACE,{"disambiguationData":[OSD([subQ0])]})]});}
            var Q35;
            {var subQ0=sQuery(id+"F3.wireOp",EDGE,"E56.trimOffspring");Q35=makeQuery(id+"F5.opChamfer","BLEND_EDGE",EDGE,{"blendedFrom":[makeQuery(id+"F4.opExtrude","CAP_EDGE",EDGE,{"disambiguationData":[OSD([subQ0])],"isStart":false}),makeQuery(id+"F4.opExtrude","SWEPT_FACE",FACE,{"disambiguationData":[OSD([subQ0])]})],"blendedInto":[makeQuery(id+"F4.opExtrude","SWEPT_FACE",FACE,{"disambiguationData":[OSD([subQ0])]})]});}
            var Q36;
            {var subQ0=sQuery(id+"F3.wireOp",EDGE,"E52.trimOffspring");Q36=makeQuery(id+"F5.opChamfer","BLEND_EDGE",EDGE,{"blendedFrom":[makeQuery(id+"F4.opExtrude","CAP_EDGE",EDGE,{"disambiguationData":[OSD([subQ0])],"isStart":false}),makeQuery(id+"F4.opExtrude","SWEPT_FACE",FACE,{"disambiguationData":[OSD([subQ0])]})],"blendedInto":[makeQuery(id+"F4.opExtrude","SWEPT_FACE",FACE,{"disambiguationData":[OSD([subQ0])]})]});}
            var Q37;
            {var subQ0=sQuery(id+"F3.wireOp",EDGE,"E26.4");Q37=makeQuery(id+"F5.opChamfer","BLEND_EDGE",EDGE,{"blendedFrom":[makeQuery(id+"F4.opExtrude","CAP_EDGE",EDGE,{"disambiguationData":[OSD([subQ0])],"isStart":false}),makeQuery(id+"F4.opExtrude","SWEPT_FACE",FACE,{"disambiguationData":[OSD([subQ0])]})],"blendedInto":[makeQuery(id+"F4.opExtrude","SWEPT_FACE",FACE,{"disambiguationData":[OSD([subQ0])]})]});}
            var Q38;
            {var subQ0=sQuery(id+"F3.wireOp",EDGE,"E26.3");Q38=makeQuery(id+"F5.opChamfer","BLEND_EDGE",EDGE,{"blendedFrom":[makeQuery(id+"F4.opExtrude","CAP_EDGE",EDGE,{"disambiguationData":[OSD([subQ0])],"isStart":false}),makeQuery(id+"F4.opExtrude","SWEPT_FACE",FACE,{"disambiguationData":[OSD([subQ0])]})],"blendedInto":[makeQuery(id+"F4.opExtrude","SWEPT_FACE",FACE,{"disambiguationData":[OSD([subQ0])]})]});}
            var Q39;
            {var subQ0=sQuery(id+"F3.wireOp",EDGE,"E50.trimOffspring");Q39=makeQuery(id+"F5.opChamfer","BLEND_EDGE",EDGE,{"blendedFrom":[makeQuery(id+"F4.opExtrude","CAP_EDGE",EDGE,{"disambiguationData":[OSD([subQ0])],"isStart":false}),makeQuery(id+"F4.opExtrude","SWEPT_FACE",FACE,{"disambiguationData":[OSD([subQ0])]})],"blendedInto":[makeQuery(id+"F4.opExtrude","SWEPT_FACE",FACE,{"disambiguationData":[OSD([subQ0])]})]});}
            fillet(context, id + "F7", {"entities" : qUnion([Q0, Q1, Q2, Q3, Q4, Q5, Q6, Q7, Q8, Q9, Q10, Q11, Q12, Q13, Q14, Q15, Q16, Q17, Q18, Q19, Q20, Q21, Q22, Q23, Q24, Q25, Q26, Q27, Q28, Q29, Q30, Q31, Q32, Q33, Q34, Q35, Q36, Q37, Q38, Q39]), "radius" : 7 * mm, "tangentPropagation" : true, "rho" : .5, "crossSection" : FilletCrossSection.CONIC, "allowEdgeOverflow" : false});
        }
        {
            var Q0;
            {var subQ0=sQuery(id+"F3.wireOp",EDGE,"E26.0");var subQ1=makeQuery(id+"F3.imprint","IMPRINT",EDGE,{"disambiguationData":[TD([[makeQuery(id+"F3.imprint","INTERSECT",VERTEX,{"derivedFrom":[subQ0,sQuery(id+"F3.wireOp",EDGE,"E51.trimOffspring")]}),-1.0]])],"derivedFrom":subQ0});Q0=makeQuery(id+"F6.opChamfer","BLEND_EDGE",EDGE,{"blendedFrom":[makeQuery(id+"F4.opExtrude","CAP_EDGE",EDGE,{"disambiguationData":[OSD([subQ0]),TDD([subQ1])],"isStart":false}),makeQuery(id+"F4.opExtrude","SWEPT_FACE",FACE,{"disambiguationData":[OSD([subQ0]),TDD([subQ1])]})],"blendedInto":[makeQuery(id+"F4.opExtrude","SWEPT_FACE",FACE,{"disambiguationData":[OSD([subQ0]),TDD([subQ1])]})]});}
            var Q1;
            {var subQ0=sQuery(id+"F3.wireOp",EDGE,"E26.0");var subQ1=makeQuery(id+"F3.imprint","IMPRINT",EDGE,{"disambiguationData":[TD([[makeQuery(id+"F3.imprint","INTERSECT",VERTEX,{"derivedFrom":[subQ0,sQuery(id+"F3.wireOp",EDGE,"E30.trimOffspring")]}),1.0]])],"derivedFrom":subQ0});Q1=makeQuery(id+"F6.opChamfer","BLEND_EDGE",EDGE,{"blendedFrom":[makeQuery(id+"F4.opExtrude","CAP_EDGE",EDGE,{"disambiguationData":[OSD([subQ0]),TDD([subQ1])],"isStart":false}),makeQuery(id+"F4.opExtrude","SWEPT_FACE",FACE,{"disambiguationData":[OSD([subQ0]),TDD([subQ1])]})],"blendedInto":[makeQuery(id+"F4.opExtrude","SWEPT_FACE",FACE,{"disambiguationData":[OSD([subQ0]),TDD([subQ1])]})]});}
            var Q2;
            {var subQ0=sQuery(id+"F3.wireOp",EDGE,"E26.0");var subQ1=makeQuery(id+"F3.imprint","IMPRINT",EDGE,{"disambiguationData":[TD([[makeQuery(id+"F3.imprint","INTERSECT",VERTEX,{"derivedFrom":[subQ0,sQuery(id+"F3.wireOp",EDGE,"E62.trimOffspring")]}),-1.0]])],"derivedFrom":subQ0});Q2=makeQuery(id+"F6.opChamfer","BLEND_EDGE",EDGE,{"blendedFrom":[makeQuery(id+"F4.opExtrude","CAP_EDGE",EDGE,{"disambiguationData":[OSD([subQ0]),TDD([subQ1])],"isStart":false}),makeQuery(id+"F4.opExtrude","SWEPT_FACE",FACE,{"disambiguationData":[OSD([subQ0]),TDD([subQ1])]})],"blendedInto":[makeQuery(id+"F4.opExtrude","SWEPT_FACE",FACE,{"disambiguationData":[OSD([subQ0]),TDD([subQ1])]})]});}
            var Q3;
            {var subQ0=sQuery(id+"F3.wireOp",EDGE,"E26.0");var subQ1=makeQuery(id+"F3.imprint","IMPRINT",EDGE,{"disambiguationData":[TD([[makeQuery(id+"F3.imprint","INTERSECT",VERTEX,{"derivedFrom":[subQ0,sQuery(id+"F3.wireOp",EDGE,"E27.trimOffspring")]}),-1.0]])],"derivedFrom":subQ0});Q3=makeQuery(id+"F6.opChamfer","BLEND_EDGE",EDGE,{"blendedFrom":[makeQuery(id+"F4.opExtrude","CAP_EDGE",EDGE,{"disambiguationData":[OSD([subQ0]),TDD([subQ1])],"isStart":false}),makeQuery(id+"F4.opExtrude","SWEPT_FACE",FACE,{"disambiguationData":[OSD([subQ0]),TDD([subQ1])]})],"blendedInto":[makeQuery(id+"F4.opExtrude","SWEPT_FACE",FACE,{"disambiguationData":[OSD([subQ0]),TDD([subQ1])]})]});}
            fillet(context, id + "F8", {"entities" : qUnion([Q0, Q1, Q2, Q3]), "radius" : 5 * mm, "tangentPropagation" : true, "allowEdgeOverflow" : false});
        }
        {
            var Q0;
            Q0=makeQuery(id+"F1.opExtrude","CAP_FACE",FACE,{"disambiguationData":[OSD([sQuery(id+"F0.wireOp",EDGE,"E0.bottom"),sQuery(id+"F0.wireOp",EDGE,"E0.top"),sQuery(id+"F0.wireOp",EDGE,"E0.left"),sQuery(id+"F0.wireOp",EDGE,"E0.right"),sQuery(id+"F0.wireOp",EDGE,"E1.filletArc"),sQuery(id+"F0.wireOp",EDGE,"E2.filletArc"),sQuery(id+"F0.wireOp",EDGE,"E3.filletArc"),sQuery(id+"F0.wireOp",EDGE,"E4.filletArc"),sQuery(id+"F0.wireOp",EDGE,"E5"),sQuery(id+"F0.wireOp",EDGE,"E6"),sQuery(id+"F0.wireOp",EDGE,"E7"),sQuery(id+"F0.wireOp",EDGE,"E8"),sQuery(id+"F0.wireOp",EDGE,"E9")])],"isStart":false});
            var sketch = newSketch(context, id + "F9", { "sketchPlane" : qUnion([Q0])});
            skArc(sketch, "E70.0.0", {"start": v(20, 16) * mm, "mid": v(18.83, 18.83) * mm, "end": v(16, 20) * mm});
            skLineSegment(sketch, "E70.0.1", {"start": v(16, 20) * mm, "end": v(-16, 20) * mm});
            skArc(sketch, "E70.0.2", {"start": v(-16, 20) * mm, "mid": v(-18.83, 18.83) * mm, "end": v(-20, 16) * mm});
            skLineSegment(sketch, "E70.0.3", {"start": v(-20, 16) * mm, "end": v(-20, -16) * mm});
            skArc(sketch, "E70.0.4", {"start": v(-20, -16) * mm, "mid": v(-18.83, -18.83) * mm, "end": v(-16, -20) * mm});
            skLineSegment(sketch, "E70.0.5", {"start": v(-16, -20) * mm, "end": v(16, -20) * mm});
            skArc(sketch, "E70.0.6", {"start": v(16, -20) * mm, "mid": v(18.83, -18.83) * mm, "end": v(20, -16) * mm});
            skLineSegment(sketch, "E70.0.7", {"start": v(20, -16) * mm, "end": v(20, 16) * mm});
            skCircle(sketch, "E71.0", {"center": v(0, 0) * mm, "radius": 18.9 * mm});
            skSolve(sketch);
        }
        {
            var Q0;
            Q0=makeQuery(id+"F1.opExtrude","CAP_FACE",FACE,{"disambiguationData":[OSD([sQuery(id+"F0.wireOp",EDGE,"E0.bottom"),sQuery(id+"F0.wireOp",EDGE,"E0.top"),sQuery(id+"F0.wireOp",EDGE,"E0.left"),sQuery(id+"F0.wireOp",EDGE,"E0.right"),sQuery(id+"F0.wireOp",EDGE,"E1.filletArc"),sQuery(id+"F0.wireOp",EDGE,"E2.filletArc"),sQuery(id+"F0.wireOp",EDGE,"E3.filletArc"),sQuery(id+"F0.wireOp",EDGE,"E4.filletArc"),sQuery(id+"F0.wireOp",EDGE,"E5"),sQuery(id+"F0.wireOp",EDGE,"E6"),sQuery(id+"F0.wireOp",EDGE,"E7"),sQuery(id+"F0.wireOp",EDGE,"E8"),sQuery(id+"F0.wireOp",EDGE,"E9")])],"isStart":false});
            var sketch = newSketch(context, id + "F10", { "sketchPlane" : qUnion([Q0])});
            skLineSegment(sketch, "E72", {"start": v(25, 6.85) * mm, "end": v(25, -8.5) * mm});
            skSolve(sketch);
        }
        {
            var Q0;
            Q0 = qSketchRegion(id + "F9", true);
            var Q1;
            Q1=sQuery(id+"F10.wireOp",EDGE,"E72");
            revolve(context, id + "F11", {"operationType" : NewBodyOperationType.ADD, "entities" : qUnion([Q0]), "axis" : qUnion([Q1]), "revolveType" : RevolveType.ONE_DIRECTION, "oppositeDirection" : true, "angle" : 70 * degree});
        }
        {
            var Q0;
            Q0=makeQuery(id+"F11.opRevolve","CAP_FACE",FACE,{"disambiguationData":[OSD([sQuery(id+"F0.wireOp",EDGE,"E5"),sQuery(id+"F0.wireOp",EDGE,"E6"),sQuery(id+"F0.wireOp",EDGE,"E7"),sQuery(id+"F0.wireOp",EDGE,"E8"),sQuery(id+"F9.wireOp",EDGE,"E70.0.0"),sQuery(id+"F9.wireOp",EDGE,"E70.0.1"),sQuery(id+"F9.wireOp",EDGE,"E70.0.2"),sQuery(id+"F9.wireOp",EDGE,"E70.0.3"),sQuery(id+"F9.wireOp",EDGE,"E70.0.4"),sQuery(id+"F9.wireOp",EDGE,"E70.0.5"),sQuery(id+"F9.wireOp",EDGE,"E70.0.6"),sQuery(id+"F9.wireOp",EDGE,"E70.0.7"),sQuery(id+"F9.wireOp",EDGE,"E71.0")])],"isStart":false});
            var sketch = newSketch(context, id + "F12", { "sketchPlane" : qUnion([Q0])});
            skCircle(sketch, "E73.0", {"center": v(0, 21.15) * mm, "radius": 18.9 * mm});
            skLineSegment(sketch, "E74.0", {"start": v(16, 41.15) * mm, "end": v(-16, 41.15) * mm});
            skArc(sketch, "E74.1", {"start": v(20, 37.15) * mm, "mid": v(18.83, 39.98) * mm, "end": v(16, 41.15) * mm});
            skLineSegment(sketch, "E74.2", {"start": v(20, 5.15) * mm, "end": v(20, 37.15) * mm});
            skArc(sketch, "E74.3", {"start": v(16, 1.15) * mm, "mid": v(18.83, 2.32) * mm, "end": v(20, 5.15) * mm});
            skLineSegment(sketch, "E74.4", {"start": v(16, 1.15) * mm, "end": v(-16, 1.15) * mm});
            skArc(sketch, "E74.5", {"start": v(-20, 5.15) * mm, "mid": v(-18.83, 2.32) * mm, "end": v(-16, 1.15) * mm});
            skLineSegment(sketch, "E74.6", {"start": v(-20, 5.15) * mm, "end": v(-20, 37.15) * mm});
            skArc(sketch, "E74.7", {"start": v(-16, 41.15) * mm, "mid": v(-18.83, 39.98) * mm, "end": v(-20, 37.15) * mm});
            skSolve(sketch);
        }
        {
            var Q0;
            Q0 = qSketchRegion(id + "F12", true);
            extrude(context, id + "F13", {"entities" : qUnion([Q0]), "operationType" : NewBodyOperationType.ADD, "depth" : 10 * mm});
        }
        {
            var Q0;
            Q0=makeQuery(id+"F13.opExtrude","CAP_FACE",FACE,{"disambiguationData":[OSD([sQuery(id+"F12.wireOp",EDGE,"E73.0"),sQuery(id+"F12.wireOp",EDGE,"E74.0"),sQuery(id+"F12.wireOp",EDGE,"E74.1"),sQuery(id+"F12.wireOp",EDGE,"E74.2"),sQuery(id+"F12.wireOp",EDGE,"E74.3"),sQuery(id+"F12.wireOp",EDGE,"E74.4"),sQuery(id+"F12.wireOp",EDGE,"E74.5"),sQuery(id+"F12.wireOp",EDGE,"E74.6"),sQuery(id+"F12.wireOp",EDGE,"E74.7")])],"isStart":false});
            var sketch = newSketch(context, id + "F14", { "sketchPlane" : qUnion([Q0])});
            skCircle(sketch, "E75", {"center": v(-16, 37.15) * mm, "radius": 1.8 * mm});
            skCircle(sketch, "E76", {"center": v(16, 37.15) * mm, "radius": 1.8 * mm});
            skCircle(sketch, "E77", {"center": v(16, 5.15) * mm, "radius": 1.8 * mm});
            skCircle(sketch, "E78", {"center": v(-16, 5.15) * mm, "radius": 1.8 * mm});
            skSolve(sketch);
        }
        {
            var Q0;
            Q0 = qSketchRegion(id + "F14", true);
            extrude(context, id + "F15", {"entities" : qUnion([Q0]), "operationType" : NewBodyOperationType.REMOVE, "oppositeDirection" : true, "depth" : 8 * mm});
        }
        {
            var Q0;
            Q0=makeQuery(id+"F11.boolean.opBoolean","SPLIT",FACE,{"disambiguationData":[TD([makeQuery(id+"F1.opExtrude","SWEPT_FACE",FACE,{"disambiguationData":[OSD([sQuery(id+"F0.wireOp",EDGE,"E8")])]})])],"derivedFrom":makeQuery(id+"F11.opRevolve","CAP_FACE",FACE,{"disambiguationData":[OSD([sQuery(id+"F9.wireOp",EDGE,"E70.0.0"),sQuery(id+"F9.wireOp",EDGE,"E70.0.1"),sQuery(id+"F9.wireOp",EDGE,"E70.0.2"),sQuery(id+"F9.wireOp",EDGE,"E70.0.3"),sQuery(id+"F9.wireOp",EDGE,"E70.0.4"),sQuery(id+"F9.wireOp",EDGE,"E70.0.5"),sQuery(id+"F9.wireOp",EDGE,"E70.0.6"),sQuery(id+"F9.wireOp",EDGE,"E70.0.7"),sQuery(id+"F9.wireOp",EDGE,"E71.0")])],"isStart":true})});
            var sketch = newSketch(context, id + "F16", { "sketchPlane" : qUnion([Q0])});
            skCircle(sketch, "E79.1", {"center": v(-16, 16) * mm, "radius": 1.8 * mm});
            skCircle(sketch, "E79.2", {"center": v(-16, -16) * mm, "radius": 1.8 * mm});
            skCircle(sketch, "E79.3", {"center": v(16, -16) * mm, "radius": 1.8 * mm});
            skCircle(sketch, "E80.0", {"center": v(16, 16) * mm, "radius": 1.8 * mm});
            skSolve(sketch);
        }
        {
            var Q0;
            Q0 = qSketchRegion(id + "F16", true);
            extrude(context, id + "F17", {"entities" : qUnion([Q0]), "operationType" : NewBodyOperationType.REMOVE, "oppositeDirection" : true, "depth" : 3 * mm});
        }
    });
